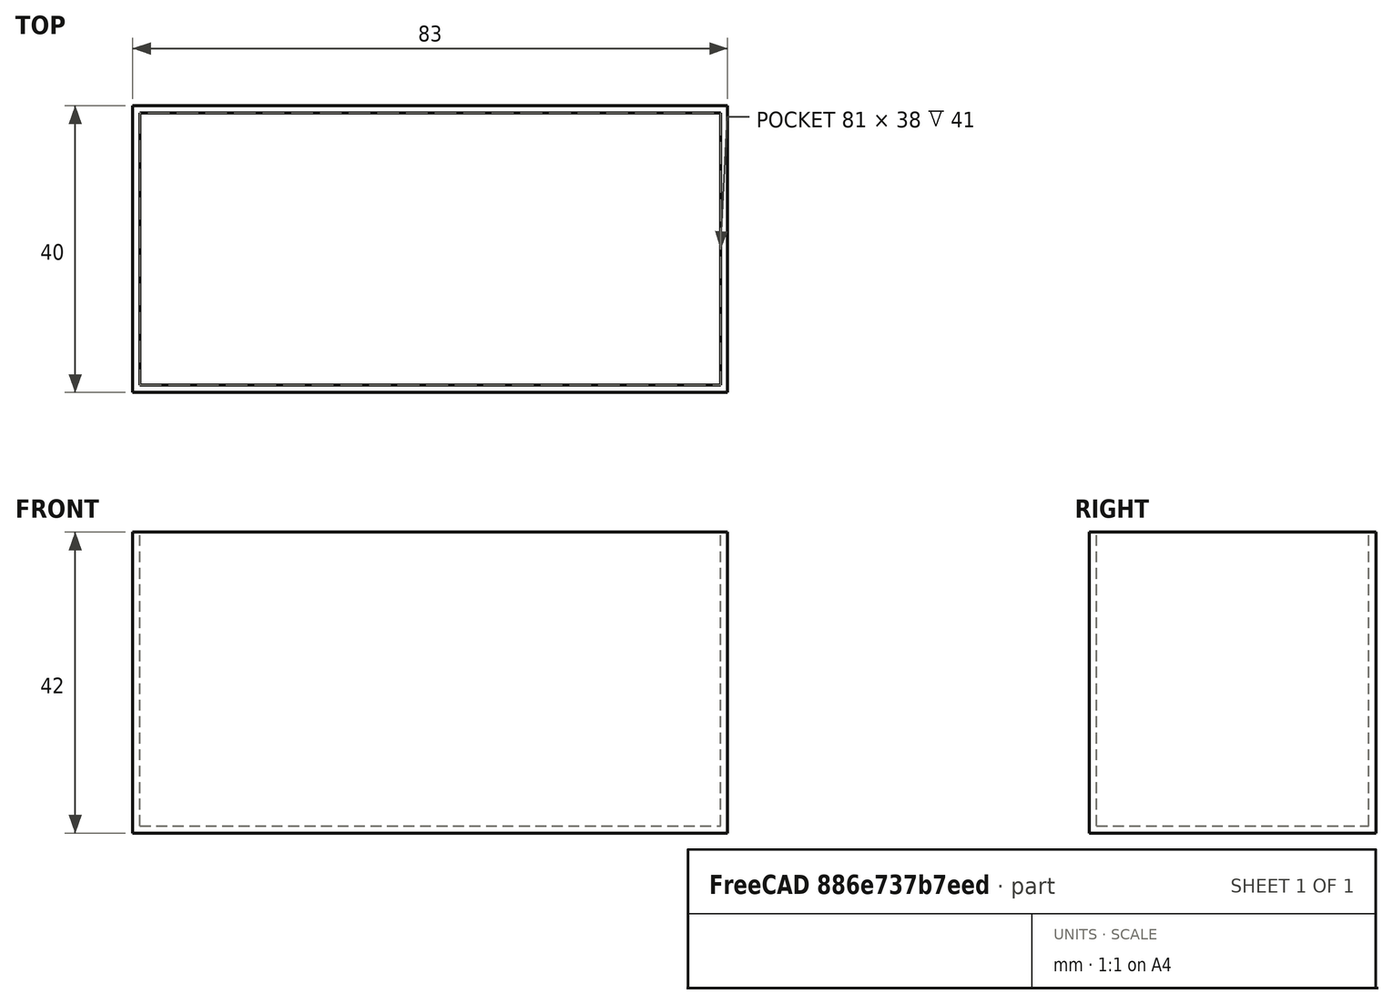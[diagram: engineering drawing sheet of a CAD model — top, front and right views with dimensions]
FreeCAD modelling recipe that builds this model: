
FCSTD DOCUMENT  (FreeCAD 1.0R39109 (Git))
Label: instaNoodContainer
License: All rights reserved
LicenseURL: https://en.wikipedia.org/wiki/All_rights_reserved
objects: PartDesign::AdditiveBox×1, PartDesign::SubtractiveBox×1, PartDesign::Body×1
note: 7 computed .brp shape members not serialized (recipe doc carries the construction recipe); baked Part::Feature solids carry a one-line shape summary decoded from their .brp

FEATURE [PartDesign::AdditiveBox] Box  label="outer"
  AttacherType = Attacher::AttachEngine3D
  AttachmentSupport = -> [XY_Plane]
  Height = 42
  Length = 83
  MapMode = 5
  Refine = true
  Suppressed = false
  Width = 40
FEATURE [PartDesign::SubtractiveBox] Box001
  AttacherType = Attacher::AttachEngine3D
  AttachmentOffset = pos=(1,1,1) rot=(0,0,1;0rad)
  AttachmentSupport = -> [XY_Plane]
  BaseFeature = -> Box
  Height = 41
  Length = 81
  MapMode = 5
  Placement = pos=(1,1,1) rot=(0,0,1;0rad)
  Refine = true
  Suppressed = false
  Width = 38
  expr: Height = <<outer>>.Height - 1 mm
  expr: Length = <<outer>>.Length - 2 mm
  expr: Width = <<outer>>.Width - 2 mm
FEATURE [PartDesign::Body] Body
  AllowCompound = false
  Group = -> [Box,Box001]
  Origin = -> Origin
  Tip = -> Box001
